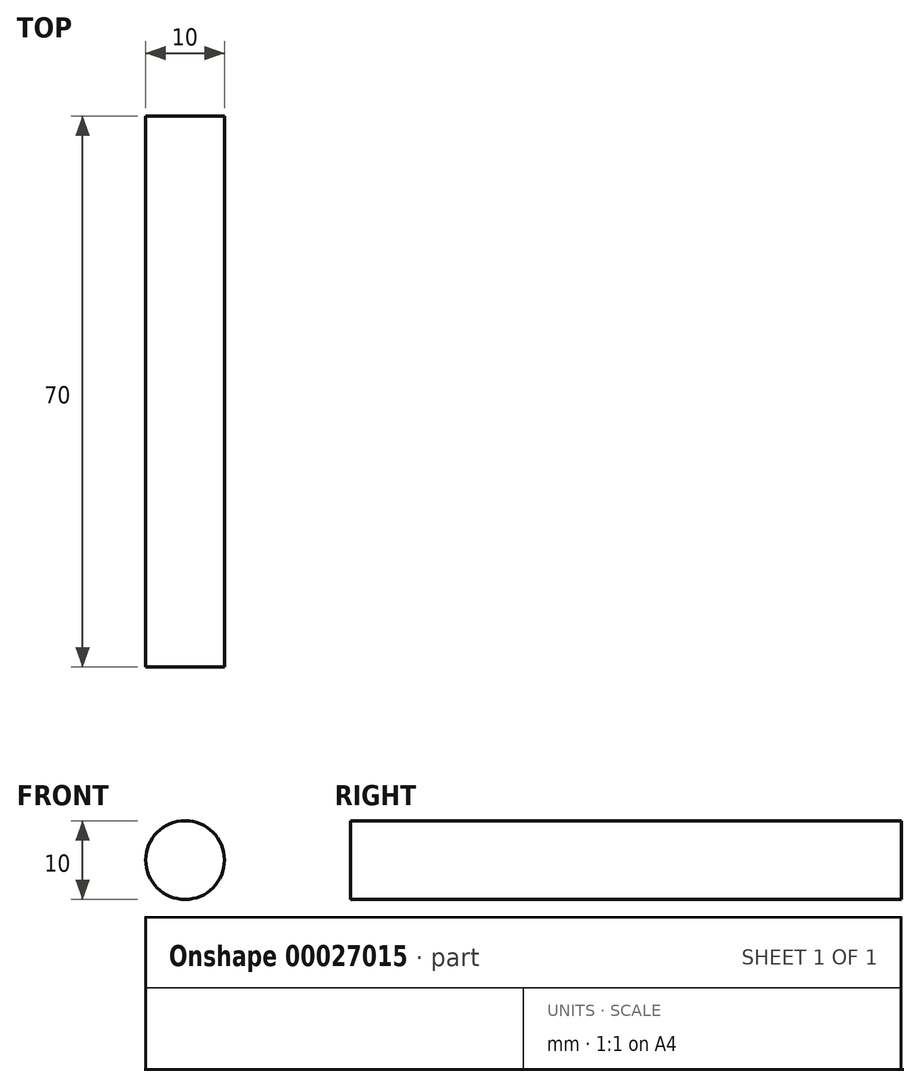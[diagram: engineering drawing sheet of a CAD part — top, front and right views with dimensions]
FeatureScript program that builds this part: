
annotation { "Feature Type Name" : "Feature", "Feature Type Description" : "" }
export const myFeature = defineFeature(function(context is Context, id is Id, definition is map)
    precondition{}
    {
        {
            var Q0;
            Q0=qCreatedBy(makeId("Front.planeOp"),FACE);
            var sketch = newSketch(context, id + "F0", { "sketchPlane" : qUnion([Q0])});
            skCircle(sketch, "E0", {"center": v(13.31, 9.82) * mm, "radius": 5 * mm});
            skSolve(sketch);
        }
        {
            var Q0;
            Q0=makeQuery(id+"F0.imprint","IMPRINT",FACE,{"disambiguationData":[TD([[makeQuery(id+"F0.imprint","IMPRINT",EDGE,{"derivedFrom":sQuery(id+"F0.wireOp",EDGE,"E0")}),1.0]])]});
            extrude(context, id + "F1", {"entities" : qUnion([Q0]), "depth" : 35 * mm, "hasSecondDirection" : true, "secondDirectionOppositeDirection" : true, "secondDirectionDepth" : 35 * mm});
        }
    });
